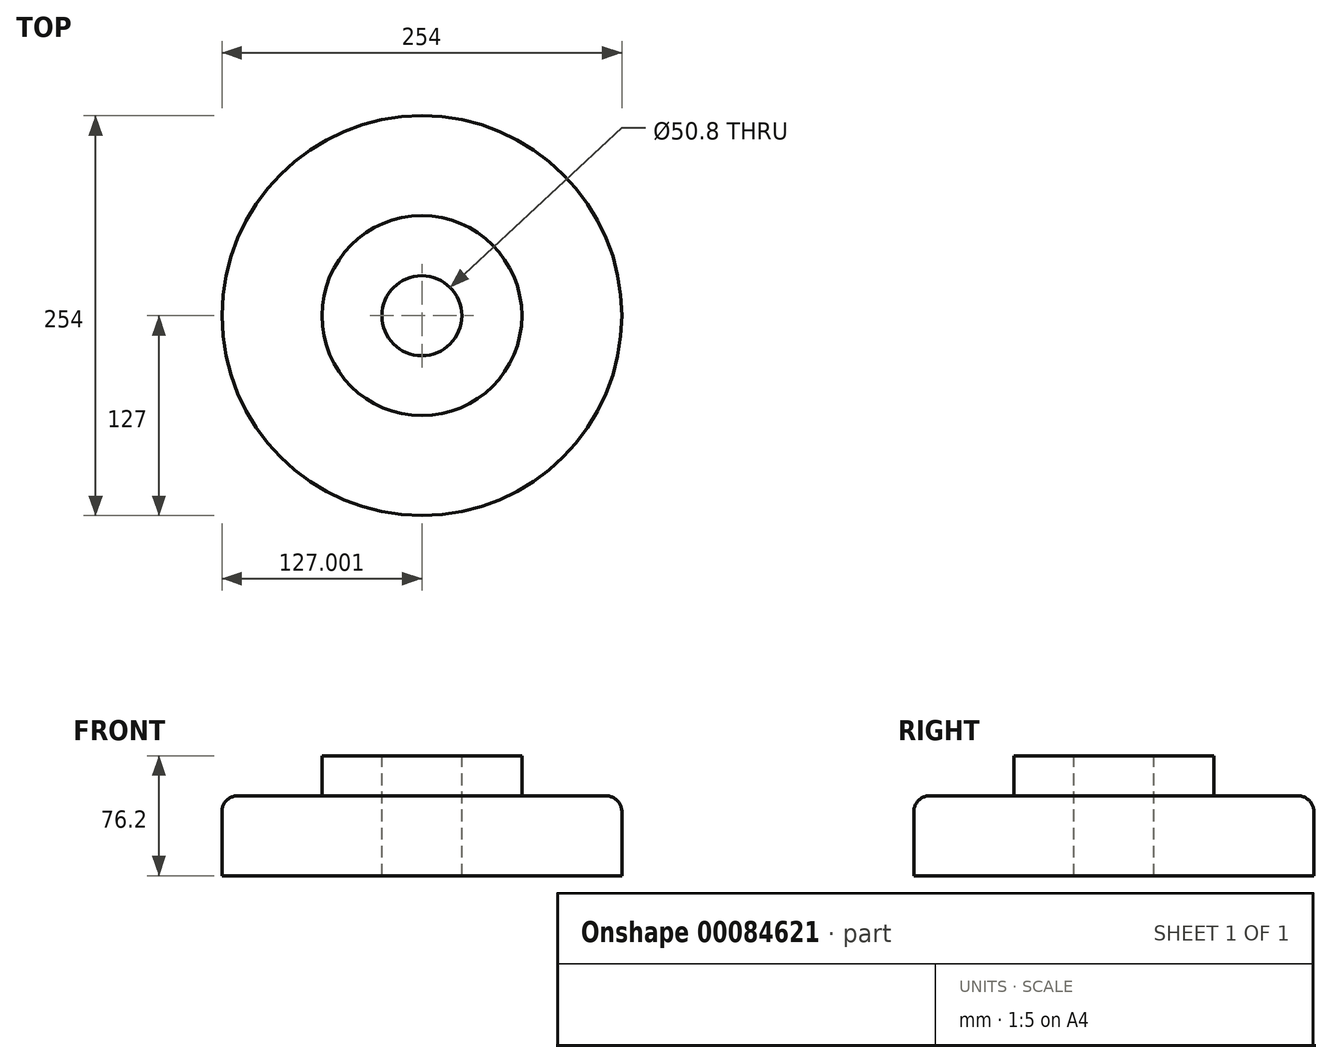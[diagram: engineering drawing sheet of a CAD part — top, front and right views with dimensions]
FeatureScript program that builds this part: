
annotation { "Feature Type Name" : "Feature", "Feature Type Description" : "" }
export const myFeature = defineFeature(function(context is Context, id is Id, definition is map)
    precondition{}
    {
        {
            var Q0;
            Q0=qCreatedBy(makeId("Front.planeOp"),FACE);
            var sketch = newSketch(context, id + "F0", { "sketchPlane" : qUnion([Q0])});
            skLineSegment(sketch, "E0", {"start": v(-58.95, -50.8) * mm, "end": v(68.05, -50.8) * mm});
            skLineSegment(sketch, "E1", {"start": v(68.05, -50.8) * mm, "end": v(68.05, 0) * mm});
            skLineSegment(sketch, "E2", {"start": v(68.05, 0) * mm, "end": v(4.55, 0) * mm});
            skLineSegment(sketch, "E3", {"start": v(4.55, 0) * mm, "end": v(4.55, 25.4) * mm});
            skLineSegment(sketch, "E4", {"start": v(4.55, 25.4) * mm, "end": v(-58.95, 25.4) * mm});
            skLineSegment(sketch, "E5", {"start": v(-58.95, 25.4) * mm, "end": v(-58.95, -50.8) * mm});
            skSolve(sketch);
        }
        {
            var Q0;
            Q0=makeQuery(id+"F0.imprint","IMPRINT",FACE,{"disambiguationData":[TD([[makeQuery(id+"F0.imprint","IMPRINT",EDGE,{"derivedFrom":sQuery(id+"F0.wireOp",EDGE,"E0")}),1.0]])]});
            var Q1;
            Q1=sQuery(id+"F0.wireOp",EDGE,"E5");
            revolve(context, id + "F1", {"entities" : qUnion([Q0]), "axis" : qUnion([Q1]), "revolveType" : RevolveType.FULL});
        }
        {
            var Q0;
            Q0=makeQuery(id+"F1.opRevolve","SWEPT_FACE",FACE,{"disambiguationData":[OSD([sQuery(id+"F0.wireOp",EDGE,"E4")])]});
            var sketch = newSketch(context, id + "F2", { "sketchPlane" : qUnion([Q0])});
            skCircle(sketch, "E6", {"center": v(-58.95, 0) * mm, "radius": 33.99 * mm});
            skSolve(sketch);
        }
        {
            var Q0;
            Q0=sQuery(id+"F2.wireOp",VERTEX,"E6.center");
            var Q1;
            Q1=makeQuery(id+"F1.opRevolve","SWEPT_BODY",BODY,{"disambiguationData":[OSD([sQuery(id+"F0.wireOp",EDGE,"E0"),sQuery(id+"F0.wireOp",EDGE,"E1"),sQuery(id+"F0.wireOp",EDGE,"E2"),sQuery(id+"F0.wireOp",EDGE,"E3"),sQuery(id+"F0.wireOp",EDGE,"E4"),sQuery(id+"F0.wireOp",EDGE,"E5")])]});
            hole(context, id + "F3", {"style" : HoleStyle.SIMPLE, "endStyle" : HoleEndStyle.THROUGH, "holeDiameter" : 50.8 * mm, "locations" : qUnion([Q0]), "scope" : qUnion([Q1]), "isTappedThrough" : true});
        }
        {
            var Q0;
            Q0=makeQuery(id+"F1.opRevolve","SWEPT_EDGE",EDGE,{"disambiguationData":[OSD([sQuery(id+"F0.wireOp",EDGE,"E1"),sQuery(id+"F0.wireOp",EDGE,"E2")])]});
            fillet(context, id + "F4", {"entities" : qUnion([Q0]), "radius" : 10.16 * mm, "tangentPropagation" : true, "allowEdgeOverflow" : false});
        }
    });
